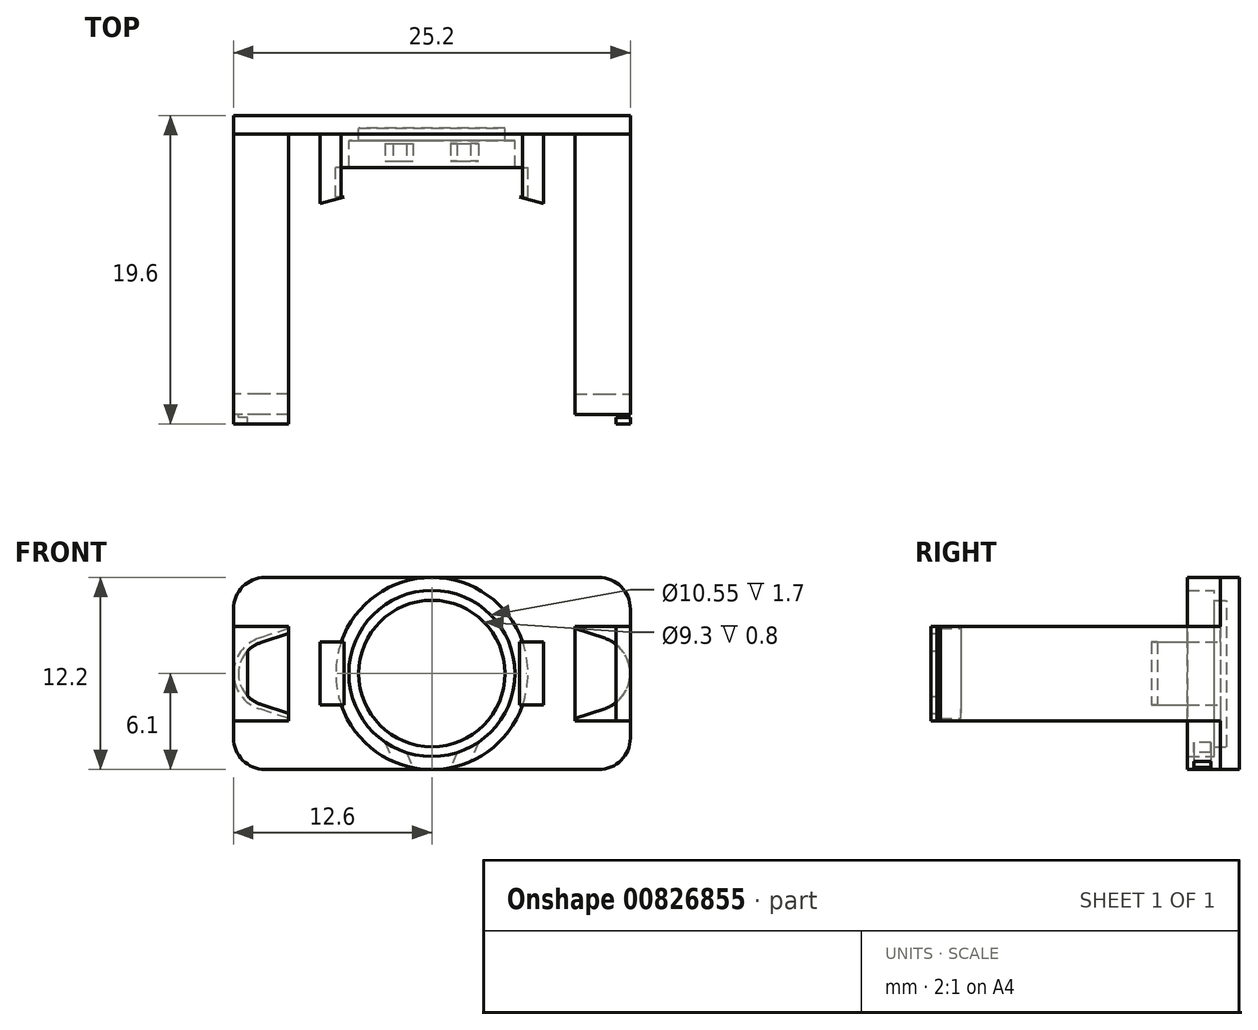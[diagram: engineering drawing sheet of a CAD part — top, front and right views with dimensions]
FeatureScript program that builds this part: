
annotation { "Feature Type Name" : "Feature", "Feature Type Description" : "" }
export const myFeature = defineFeature(function(context is Context, id is Id, definition is map)
    precondition{}
    {
        {
            var Q0;
            Q0=qCreatedBy(makeId("Front.planeOp"),FACE);
            var sketch = newSketch(context, id + "F0", { "sketchPlane" : qUnion([Q0])});
            skCircle(sketch, "E0", {"center": v(0, 0) * mm, "radius": 5 * mm});
            skCircle(sketch, "E1", {"center": v(0, 0) * mm, "radius": 6.1 * mm});
            skSolve(sketch);
        }
        {
            var Q0;
            Q0=makeQuery(id+"F0.imprint","IMPRINT",FACE,{"disambiguationData":[TD([[makeQuery(id+"F0.imprint","IMPRINT",EDGE,{"derivedFrom":sQuery(id+"F0.wireOp",EDGE,"E0")}),-1.0]])]});
            var Q1;
            Q1=makeQuery(id+"F0.imprint","IMPRINT",FACE,{"disambiguationData":[TD([[makeQuery(id+"F0.imprint","IMPRINT",EDGE,{"derivedFrom":sQuery(id+"F0.wireOp",EDGE,"E0")}),1.0]])]});
            extrude(context, id + "F1", {"entities" : qUnion([Q0, Q1]), "depth" : 0.8 * mm, "offsetDistance" : 25 * mm});
        }
        {
            var Q0;
            Q0=makeQuery(id+"F1.opExtrude","CAP_FACE",FACE,{"disambiguationData":[OSD([sQuery(id+"F0.wireOp",EDGE,"E1")])],"isStart":false});
            var sketch = newSketch(context, id + "F2", { "sketchPlane" : qUnion([Q0])});
            skCircle(sketch, "E2", {"center": v(0, 0) * mm, "radius": 5.45 * mm});
            skCircle(sketch, "E3", {"center": v(0, 0) * mm, "radius": 6.1 * mm});
            skSolve(sketch);
        }
        {
            var Q0;
            Q0=makeQuery(id+"F2.imprint","IMPRINT",FACE,{"disambiguationData":[TD([[makeQuery(id+"F2.imprint","IMPRINT",EDGE,{"derivedFrom":sQuery(id+"F2.wireOp",EDGE,"E2")}),-1.0]])]});
            extrude(context, id + "F3", {"entities" : qUnion([Q0]), "operationType" : NewBodyOperationType.ADD, "depth" : 2.5 * mm, "offsetDistance" : 25 * mm});
        }
        {
            var Q0;
            Q0=makeQuery(id+"F1.opExtrude","CAP_FACE",FACE,{"disambiguationData":[OSD([sQuery(id+"F0.wireOp",EDGE,"E1")])],"isStart":false});
            var sketch = newSketch(context, id + "F4", { "sketchPlane" : qUnion([Q0])});
            skCircle(sketch, "E4", {"center": v(0, 0) * mm, "radius": 4.65 * mm});
            skSolve(sketch);
        }
        {
            var Q0;
            Q0=makeQuery(id+"F4.imprint","IMPRINT",FACE,{"disambiguationData":[TD([[makeQuery(id+"F4.imprint","IMPRINT",EDGE,{"derivedFrom":sQuery(id+"F4.wireOp",EDGE,"E4")}),-1.0]])]});
            extrude(context, id + "F5", {"entities" : qUnion([Q0]), "operationType" : NewBodyOperationType.ADD, "depth" : 0.8 * mm, "offsetDistance" : 25 * mm});
        }
        {
            var Q0;
            Q0=makeQuery(id+"F5.opExtrude","CAP_FACE",FACE,{"disambiguationData":[OSD([sQuery(id+"F2.wireOp",EDGE,"E2"),sQuery(id+"F4.wireOp",EDGE,"E4")])],"isStart":false});
            var sketch = newSketch(context, id + "F6", { "sketchPlane" : qUnion([Q0])});
            skCircle(sketch, "E5", {"center": v(0, 0) * mm, "radius": 5.28 * mm});
            skSolve(sketch);
        }
        {
            var Q0;
            Q0=makeQuery(id+"F6.imprint","IMPRINT",FACE,{"disambiguationData":[TD([[makeQuery(id+"F6.imprint","IMPRINT",EDGE,{"derivedFrom":sQuery(id+"F6.wireOp",EDGE,"E5")}),-1.0]])]});
            extrude(context, id + "F7", {"entities" : qUnion([Q0]), "operationType" : NewBodyOperationType.ADD, "depth" : 1.7 * mm, "offsetDistance" : 25 * mm});
        }
        {
            var Q0;
            Q0=makeQuery(id+"F3.opExtrude","CAP_FACE",FACE,{"disambiguationData":[OSD([sQuery(id+"F2.wireOp",EDGE,"E2"),sQuery(id+"F2.wireOp",EDGE,"E3")])],"isStart":false});
            var sketch = newSketch(context, id + "F8", { "sketchPlane" : qUnion([Q0])});
            skLineSegment(sketch, "E6", {"start": v(-1.6, -5.03) * mm, "end": v(-1.2, -5.98) * mm});
            skLineSegment(sketch, "E7", {"start": v(-2.96, -4.37) * mm, "end": v(-2.45, -5.59) * mm});
            skLineSegment(sketch, "E8.MirrorCS", {"start": v(1.6, -5.03) * mm, "end": v(1.2, -5.98) * mm});
            skLineSegment(sketch, "E9.MirrorCS", {"start": v(2.96, -4.37) * mm, "end": v(2.45, -5.59) * mm});
            skSolve(sketch);
        }
        {
            var Q0;
            {var subQ0=sQuery(id+"F8.wireOp",EDGE,"E6");Q0=makeQuery(id+"F8.imprint","IMPRINT",FACE,{"disambiguationData":[TD([[makeQuery(id+"F8.imprint","IMPRINT",EDGE,{"derivedFrom":subQ0}),-1.0]])]});}
            var Q1;
            {var subQ0=sQuery(id+"F8.wireOp",EDGE,"E8.MirrorCS");Q1=makeQuery(id+"F8.imprint","IMPRINT",FACE,{"disambiguationData":[TD([[makeQuery(id+"F8.imprint","IMPRINT",EDGE,{"derivedFrom":subQ0}),1.0]])]});}
            extrude(context, id + "F9", {"entities" : qUnion([Q0, Q1]), "operationType" : NewBodyOperationType.REMOVE, "oppositeDirection" : true, "depth" : 1.5 * mm, "offsetDistance" : 25 * mm});
        }
        {
            var Q0;
            {var subQ0=sQuery(id+"F2.wireOp",EDGE,"E3");var subQ1=sQuery(id+"F2.wireOp",EDGE,"E2");Q0=makeQuery(id+"F9.boolean.opBoolean","SPLIT",FACE,{"disambiguationData":[TD([makeQuery(id+"F9.opExtrude","SWEPT_FACE",FACE,{"disambiguationData":[OSD([sQuery(id+"F8.wireOp",EDGE,"E7")])]})])],"derivedFrom":makeQuery(id+"F3.opExtrude","CAP_FACE",FACE,{"disambiguationData":[OSD([subQ1,subQ0])],"isStart":false})});}
            var sketch = newSketch(context, id + "F10", { "sketchPlane" : qUnion([Q0])});
            skArc(sketch, "E10", {"start": v(-2.45, -5.59) * mm, "mid": v(-1.84, -5.82) * mm, "end": v(-1.2, -5.98) * mm});
            skLineSegment(sketch, "E11", {"start": v(-2.96, -4.37) * mm, "end": v(-2.45, -5.59) * mm});
            skLineSegment(sketch, "E12", {"start": v(-1.6, -5.03) * mm, "end": v(-1.2, -5.98) * mm});
            skLineSegment(sketch, "E13.MirrorCS", {"start": v(2.96, -4.37) * mm, "end": v(2.45, -5.59) * mm});
            skArc(sketch, "E14.MirrorCS", {"start": v(2.45, -5.59) * mm, "mid": v(1.84, -5.82) * mm, "end": v(1.2, -5.98) * mm});
            skLineSegment(sketch, "E15.MirrorCS", {"start": v(1.6, -5.03) * mm, "end": v(1.2, -5.98) * mm});
            skPoint(sketch, "E16.MirrorCS.end.orphan", {"position": v(1.6, -5.03) * mm});
            skPoint(sketch, "E16.MirrorCS.start.orphan", {"position": v(2.96, -4.37) * mm});
            skPoint(sketch, "E17.MirrorCS.end.orphan", {"position": v(-2.96, -4.37) * mm});
            skPoint(sketch, "E17.MirrorCS.start.orphan", {"position": v(-1.6, -5.03) * mm});
            skSolve(sketch);
        }
        {
            var Q0;
            {var subQ0=sQuery(id+"F8.wireOp",EDGE,"E6");Q0=makeQuery(id+"F8.imprint","IMPRINT",FACE,{"disambiguationData":[TD([[makeQuery(id+"F8.imprint","IMPRINT",EDGE,{"derivedFrom":subQ0}),-1.0]])]});}
            var Q1;
            {var subQ0=sQuery(id+"F8.wireOp",EDGE,"E8.MirrorCS");Q1=makeQuery(id+"F8.imprint","IMPRINT",FACE,{"disambiguationData":[TD([[makeQuery(id+"F8.imprint","IMPRINT",EDGE,{"derivedFrom":subQ0}),1.0]])]});}
            extrude(context, id + "F11", {"entities" : qUnion([Q0, Q1]), "operationType" : NewBodyOperationType.ADD, "oppositeDirection" : true, "depth" : 0.4 * mm, "offsetDistance" : 25 * mm});
        }
        {
            var Q0;
            Q0=makeQuery(id+"F1.opExtrude","CAP_FACE",FACE,{"disambiguationData":[OSD([sQuery(id+"F0.wireOp",EDGE,"E1")])],"isStart":true});
            var sketch = newSketch(context, id + "F12", { "sketchPlane" : qUnion([Q0])});
            skLineSegment(sketch, "E18.bottom", {"start": v(-12.6, -6.1) * mm, "end": v(12.6, -6.1) * mm});
            skLineSegment(sketch, "E18.top", {"start": v(-12.6, 6.1) * mm, "end": v(12.6, 6.1) * mm});
            skLineSegment(sketch, "E18.left", {"start": v(-12.6, -6.1) * mm, "end": v(-12.6, 6.1) * mm});
            skLineSegment(sketch, "E18.right", {"start": v(12.6, -6.1) * mm, "end": v(12.6, 6.1) * mm});
            skPoint(sketch, "E18.middle", {"position": v(0, 0) * mm});
            skSolve(sketch);
        }
        {
            var Q0;
            {var subQ0=sQuery(id+"F12.wireOp",EDGE,"E18.right");Q0=makeQuery(id+"F12.imprint","IMPRINT",FACE,{"disambiguationData":[TD([[makeQuery(id+"F12.imprint","IMPRINT",EDGE,{"derivedFrom":subQ0}),1.0]])]});}
            var Q1;
            {var subQ0=sQuery(id+"F12.wireOp",EDGE,"E18.left");Q1=makeQuery(id+"F12.imprint","IMPRINT",FACE,{"disambiguationData":[TD([[makeQuery(id+"F12.imprint","IMPRINT",EDGE,{"derivedFrom":subQ0}),-1.0]])]});}
            extrude(context, id + "F13", {"entities" : qUnion([Q0, Q1]), "operationType" : NewBodyOperationType.ADD, "oppositeDirection" : true, "depth" : 1.2 * mm, "offsetDistance" : 25 * mm});
        }
        {
            var Q0;
            Q0=makeQuery(id+"F13.opExtrude","SWEPT_EDGE",EDGE,{"disambiguationData":[OSD([sQuery(id+"F12.wireOp",EDGE,"E18.bottom"),sQuery(id+"F12.wireOp",EDGE,"E18.right")])]});
            var Q1;
            Q1=makeQuery(id+"F13.opExtrude","SWEPT_EDGE",EDGE,{"disambiguationData":[OSD([sQuery(id+"F12.wireOp",EDGE,"E18.bottom"),sQuery(id+"F12.wireOp",EDGE,"E18.left")])]});
            var Q2;
            Q2=makeQuery(id+"F13.opExtrude","SWEPT_EDGE",EDGE,{"disambiguationData":[OSD([sQuery(id+"F12.wireOp",EDGE,"E18.top"),sQuery(id+"F12.wireOp",EDGE,"E18.left")])]});
            var Q3;
            Q3=makeQuery(id+"F13.opExtrude","SWEPT_EDGE",EDGE,{"disambiguationData":[OSD([sQuery(id+"F12.wireOp",EDGE,"E18.top"),sQuery(id+"F12.wireOp",EDGE,"E18.right")])]});
            fillet(context, id + "F14", {"entities" : qUnion([Q0, Q1, Q2, Q3]), "radius" : 2 * mm, "tangentPropagation" : true, "allowEdgeOverflow" : false});
        }
        {
            var Q0;
            Q0=makeQuery(id+"F13.opExtrude","CAP_FACE",FACE,{"disambiguationData":[OSD([sQuery(id+"F0.wireOp",EDGE,"E1"),sQuery(id+"F12.wireOp",EDGE,"E18.bottom"),sQuery(id+"F12.wireOp",EDGE,"E18.top"),sQuery(id+"F12.wireOp",EDGE,"E18.right")])],"isStart":false});
            var sketch = newSketch(context, id + "F15", { "sketchPlane" : qUnion([Q0])});
            skLineSegment(sketch, "E19", {"start": v(-12.6, 3) * mm, "end": v(-9.1, 3) * mm});
            skLineSegment(sketch, "E20", {"start": v(-9.1, 3) * mm, "end": v(-9.1, -3) * mm});
            skLineSegment(sketch, "E21", {"start": v(-9.1, -3) * mm, "end": v(-12.6, -3) * mm});
            skLineSegment(sketch, "E22", {"start": v(-7.1, 2) * mm, "end": v(-7.1, -2) * mm});
            skLineSegment(sketch, "E23", {"start": v(-7.1, -2) * mm, "end": v(-5.76, -2) * mm});
            skLineSegment(sketch, "E24", {"start": v(-7.1, 2) * mm, "end": v(-5.76, 2) * mm});
            skSolve(sketch);
        }
        {
            var Q0;
            {var subQ0=sQuery(id+"F15.wireOp",EDGE,"E19");Q0=makeQuery(id+"F15.imprint","IMPRINT",FACE,{"disambiguationData":[TD([[makeQuery(id+"F15.imprint","IMPRINT",EDGE,{"derivedFrom":subQ0}),-1.0]])]});}
            extrude(context, id + "F16", {"entities" : qUnion([Q0]), "operationType" : NewBodyOperationType.ADD, "depth" : 16.5 * mm, "offsetDistance" : 25 * mm});
        }
        {
            var Q0;
            Q0=makeQuery(id+"F13.opExtrude","CAP_FACE",FACE,{"disambiguationData":[OSD([sQuery(id+"F0.wireOp",EDGE,"E1"),sQuery(id+"F12.wireOp",EDGE,"E18.bottom"),sQuery(id+"F12.wireOp",EDGE,"E18.top"),sQuery(id+"F12.wireOp",EDGE,"E18.left")])],"isStart":false});
            var sketch = newSketch(context, id + "F17", { "sketchPlane" : qUnion([Q0])});
            skLineSegment(sketch, "E25", {"start": v(12.6, 3) * mm, "end": v(9.1, 3) * mm});
            skLineSegment(sketch, "E26", {"start": v(9.1, 3) * mm, "end": v(9.1, -3) * mm});
            skLineSegment(sketch, "E27", {"start": v(9.1, -3) * mm, "end": v(12.6, -3) * mm});
            skLineSegment(sketch, "E28", {"start": v(7.1, 2) * mm, "end": v(7.1, -2) * mm});
            skLineSegment(sketch, "E29", {"start": v(7.1, -2) * mm, "end": v(5.76, -2) * mm});
            skLineSegment(sketch, "E30", {"start": v(7.1, 2) * mm, "end": v(5.76, 2) * mm});
            skSolve(sketch);
        }
        {
            var Q0;
            {var subQ0=sQuery(id+"F17.wireOp",EDGE,"E25");Q0=makeQuery(id+"F17.imprint","IMPRINT",FACE,{"disambiguationData":[TD([[makeQuery(id+"F17.imprint","IMPRINT",EDGE,{"derivedFrom":subQ0}),1.0]])]});}
            extrude(context, id + "F18", {"entities" : qUnion([Q0]), "operationType" : NewBodyOperationType.ADD, "depth" : 16.5 * mm, "offsetDistance" : 25 * mm});
        }
        {
            var Q0;
            Q0=makeQuery(id+"F17.imprint","IMPRINT",FACE,{"disambiguationData":[TD([[makeQuery(id+"F17.imprint","IMPRINT",EDGE,{"derivedFrom":sQuery(id+"F17.wireOp",EDGE,"E28")}),-1.0]])]});
            var Q1;
            Q1=makeQuery(id+"F15.imprint","IMPRINT",FACE,{"disambiguationData":[TD([[makeQuery(id+"F15.imprint","IMPRINT",EDGE,{"derivedFrom":sQuery(id+"F15.wireOp",EDGE,"E22")}),1.0]])]});
            extrude(context, id + "F19", {"entities" : qUnion([Q0, Q1]), "operationType" : NewBodyOperationType.ADD, "depth" : 4 * mm, "offsetDistance" : 25 * mm});
        }
        {
            var Q0;
            Q0=makeQuery(id+"F19.opExtrude","SWEPT_FACE",FACE,{"disambiguationData":[OSD([sQuery(id+"F15.wireOp",EDGE,"E23")])]});
            var sketch = newSketch(context, id + "F20", { "sketchPlane" : qUnion([Q0])});
            skLineSegment(sketch, "E31", {"start": v(-7.1, 5.2) * mm, "end": v(-7.1, 5.6) * mm});
            skLineSegment(sketch, "E32", {"start": v(-5.76, 5.2) * mm, "end": v(-5.66, 5.2) * mm});
            skLineSegment(sketch, "E33", {"start": v(-5.66, 5.2) * mm, "end": v(-7.1, 5.6) * mm});
            skSolve(sketch);
        }
        {
            var Q0;
            Q0=makeQuery(id+"F20.imprint","IMPRINT",FACE,{"disambiguationData":[TD([[makeQuery(id+"F20.imprint","IMPRINT",EDGE,{"derivedFrom":sQuery(id+"F20.wireOp",EDGE,"E31")}),-1.0]])]});
            extrude(context, id + "F21", {"entities" : qUnion([Q0]), "operationType" : NewBodyOperationType.ADD, "oppositeDirection" : true, "depth" : 4 * mm, "offsetDistance" : 25 * mm});
        }
        {
            var Q0;
            Q0=makeQuery(id+"F19.opExtrude","SWEPT_FACE",FACE,{"disambiguationData":[OSD([sQuery(id+"F17.wireOp",EDGE,"E29")])]});
            var sketch = newSketch(context, id + "F22", { "sketchPlane" : qUnion([Q0])});
            skLineSegment(sketch, "E34", {"start": v(7.1, 5.2) * mm, "end": v(7.1, 5.6) * mm});
            skLineSegment(sketch, "E35", {"start": v(5.76, 5.2) * mm, "end": v(5.66, 5.2) * mm});
            skLineSegment(sketch, "E36", {"start": v(5.66, 5.2) * mm, "end": v(7.1, 5.6) * mm});
            skSolve(sketch);
        }
        {
            var Q0;
            Q0=makeQuery(id+"F22.imprint","IMPRINT",FACE,{"disambiguationData":[TD([[makeQuery(id+"F22.imprint","IMPRINT",EDGE,{"derivedFrom":sQuery(id+"F22.wireOp",EDGE,"E34")}),1.0]])]});
            extrude(context, id + "F23", {"entities" : qUnion([Q0]), "operationType" : NewBodyOperationType.ADD, "oppositeDirection" : true, "depth" : 4 * mm, "offsetDistance" : 25 * mm});
        }
        {
            var Q0;
            {var subQ0=sQuery(id+"F15.wireOp",EDGE,"E23");Q0=makeQuery(id+"F21.boolean.opBoolean","MERGE",FACE,{"derivedFrom":[makeQuery(id+"F19.opExtrude","SWEPT_FACE",FACE,{"disambiguationData":[OSD([subQ0])]}),makeQuery(id+"F21.opExtrude","CAP_FACE",FACE,{"disambiguationData":[OSD([subQ0,sQuery(id+"F20.wireOp",EDGE,"E31"),sQuery(id+"F20.wireOp",EDGE,"scbSYdZa-IKE8-HjIA-PmpS-5iz6sRiiHXsu")])],"isStart":true})]});}
            var sketch = newSketch(context, id + "F24", { "sketchPlane" : qUnion([Q0])});
            skLineSegment(sketch, "E37", {"start": v(-5.76, 5.2) * mm, "end": v(-5.56, 5.2) * mm});
            skLineSegment(sketch, "E38", {"start": v(-5.56, 5.2) * mm, "end": v(-7.1, 5.6) * mm});
            skSolve(sketch);
        }
        {
            var Q0;
            Q0=makeQuery(id+"F24.imprint","IMPRINT",FACE,{"disambiguationData":[TD([[makeQuery(id+"F24.imprint","IMPRINT",EDGE,{"derivedFrom":sQuery(id+"F24.wireOp",EDGE,"E37")}),1.0]])]});
            extrude(context, id + "F25", {"entities" : qUnion([Q0]), "operationType" : NewBodyOperationType.ADD, "oppositeDirection" : true, "depth" : 4 * mm, "offsetDistance" : 25 * mm});
        }
        {
            var Q0;
            {var subQ0=sQuery(id+"F17.wireOp",EDGE,"E29");Q0=makeQuery(id+"F23.boolean.opBoolean","MERGE",FACE,{"derivedFrom":[makeQuery(id+"F19.opExtrude","SWEPT_FACE",FACE,{"disambiguationData":[OSD([subQ0])]}),makeQuery(id+"F23.opExtrude","CAP_FACE",FACE,{"disambiguationData":[OSD([subQ0,sQuery(id+"F22.wireOp",EDGE,"E34"),sQuery(id+"F22.wireOp",EDGE,"OUZQXp2e-nWsZ-sgYy-KXVV-Yu3MqT17kAb9")])],"isStart":true})]});}
            var sketch = newSketch(context, id + "F26", { "sketchPlane" : qUnion([Q0])});
            skLineSegment(sketch, "E39", {"start": v(5.76, 5.2) * mm, "end": v(5.56, 5.2) * mm});
            skLineSegment(sketch, "E40", {"start": v(5.56, 5.2) * mm, "end": v(7.1, 5.6) * mm});
            skSolve(sketch);
        }
        {
            var Q0;
            Q0=makeQuery(id+"F26.imprint","IMPRINT",FACE,{"disambiguationData":[TD([[makeQuery(id+"F26.imprint","IMPRINT",EDGE,{"derivedFrom":sQuery(id+"F26.wireOp",EDGE,"E39")}),-1.0]])]});
            extrude(context, id + "F27", {"entities" : qUnion([Q0]), "operationType" : NewBodyOperationType.ADD, "oppositeDirection" : true, "depth" : 4 * mm, "offsetDistance" : 25 * mm});
        }
        {
            var Q0;
            Q0=makeQuery(id+"F18.opExtrude","CAP_FACE",FACE,{"disambiguationData":[OSD([sQuery(id+"F12.wireOp",EDGE,"E18.left"),sQuery(id+"F17.wireOp",EDGE,"E25"),sQuery(id+"F17.wireOp",EDGE,"E26"),sQuery(id+"F17.wireOp",EDGE,"E27")])],"isStart":false});
            var sketch = newSketch(context, id + "F28", { "sketchPlane" : qUnion([Q0])});
            skLineSegment(sketch, "E41", {"start": v(9.1, 2.85) * mm, "end": v(10.95, 2.25) * mm});
            skArc(sketch, "E42", {"start": v(10.95, -2.25) * mm, "mid": v(12.59, 0) * mm, "end": v(10.95, 2.25) * mm});
            skLineSegment(sketch, "E43.MirrorCS", {"start": v(9.1, -2.85) * mm, "end": v(10.95, -2.25) * mm});
            skSolve(sketch);
        }
        {
            var Q0;
            {var subQ2=sQuery(id+"F28.wireOp",EDGE,"E41");Q0=makeQuery(id+"F28.imprint","IMPRINT",FACE,{"disambiguationData":[TD([[makeQuery(id+"F28.imprint","IMPRINT",EDGE,{"derivedFrom":subQ2}),1.0]])]});}
            extrude(context, id + "F29", {"entities" : qUnion([Q0]), "operationType" : NewBodyOperationType.ADD, "depth" : 1.3 * mm, "offsetDistance" : 25 * mm});
        }
        {
            var Q0;
            Q0=makeQuery(id+"F16.opExtrude","CAP_FACE",FACE,{"disambiguationData":[OSD([sQuery(id+"F12.wireOp",EDGE,"E18.right"),sQuery(id+"F15.wireOp",EDGE,"E19"),sQuery(id+"F15.wireOp",EDGE,"E20"),sQuery(id+"F15.wireOp",EDGE,"E21")])],"isStart":false});
            var sketch = newSketch(context, id + "F30", { "sketchPlane" : qUnion([Q0])});
            skLineSegment(sketch, "E44", {"start": v(-9.1, 2.85) * mm, "end": v(-10.95, 2.25) * mm});
            skLineSegment(sketch, "E45.MirrorCS", {"start": v(-9.1, -2.85) * mm, "end": v(-10.95, -2.25) * mm});
            skArc(sketch, "E46", {"start": v(-10.95, 2.25) * mm, "mid": v(-12.59, 0) * mm, "end": v(-10.95, -2.25) * mm});
            skSolve(sketch);
        }
        {
            var Q0;
            {var subQ2=sQuery(id+"F30.wireOp",EDGE,"E44");Q0=makeQuery(id+"F30.imprint","IMPRINT",FACE,{"disambiguationData":[TD([[makeQuery(id+"F30.imprint","IMPRINT",EDGE,{"derivedFrom":subQ2}),-1.0]])]});}
            extrude(context, id + "F31", {"entities" : qUnion([Q0]), "operationType" : NewBodyOperationType.ADD, "depth" : 1.3 * mm, "offsetDistance" : 25 * mm});
        }
        {
            var Q0;
            Q0=makeQuery(id+"F31.opExtrude","CAP_FACE",FACE,{"disambiguationData":[OSD([sQuery(id+"F12.wireOp",EDGE,"E18.right"),sQuery(id+"F15.wireOp",EDGE,"E19"),sQuery(id+"F15.wireOp",EDGE,"E20"),sQuery(id+"F15.wireOp",EDGE,"E21"),sQuery(id+"F30.wireOp",EDGE,"E44"),sQuery(id+"F30.wireOp",EDGE,"E45.MirrorCS"),sQuery(id+"F30.wireOp",EDGE,"E46")])],"isStart":false});
            var sketch = newSketch(context, id + "F32", { "sketchPlane" : qUnion([Q0])});
            skLineSegment(sketch, "E47", {"start": v(-12.6, 3) * mm, "end": v(-12.6, -3) * mm});
            skLineSegment(sketch, "E48", {"start": v(-12.6, -3) * mm, "end": v(-9.1, -3) * mm});
            skLineSegment(sketch, "E49.0", {"start": v(-9.1, -2.53) * mm, "end": v(-10.86, -1.96) * mm});
            skArc(sketch, "E49.1", {"start": v(-10.86, 1.96) * mm, "mid": v(-12.3, 0) * mm, "end": v(-10.86, -1.96) * mm});
            skLineSegment(sketch, "E49.2", {"start": v(-9.1, 2.53) * mm, "end": v(-10.86, 1.96) * mm});
            skArc(sketch, "E50.MirrorCS", {"start": v(10.86, 1.96) * mm, "mid": v(12.3, 0) * mm, "end": v(10.86, -1.96) * mm});
            skLineSegment(sketch, "E51.MirrorCS", {"start": v(9.1, 2.53) * mm, "end": v(10.86, 1.96) * mm});
            skLineSegment(sketch, "E52.MirrorCS", {"start": v(9.1, -2.53) * mm, "end": v(10.86, -1.96) * mm});
            skLineSegment(sketch, "E53.MirrorCS", {"start": v(12.6, -3) * mm, "end": v(9.1, -3) * mm});
            skLineSegment(sketch, "E54.MirrorCS", {"start": v(12.6, 3) * mm, "end": v(12.6, -3) * mm});
            skLineSegment(sketch, "E55", {"start": v(-12.6, 3) * mm, "end": v(-9.1, 3) * mm});
            skLineSegment(sketch, "E56.MirrorCS", {"start": v(12.6, 3) * mm, "end": v(9.1, 3) * mm});
            skLineSegment(sketch, "E57", {"start": v(-9.1, 2.53) * mm, "end": v(-9.1, 3) * mm});
            skLineSegment(sketch, "E58", {"start": v(-9.1, -2.53) * mm, "end": v(-9.1, -3) * mm});
            skLineSegment(sketch, "E59.MirrorCS", {"start": v(9.1, -2.53) * mm, "end": v(9.1, -3) * mm});
            skLineSegment(sketch, "E60.MirrorCS", {"start": v(9.1, 2.53) * mm, "end": v(9.1, 3) * mm});
            skSolve(sketch);
        }
        {
            var Q0;
            {var subQ3=sQuery(id+"F32.wireOp",EDGE,"E49.0");Q0=makeQuery(id+"F32.imprint","IMPRINT",FACE,{"disambiguationData":[TD([[makeQuery(id+"F32.imprint","IMPRINT",EDGE,{"derivedFrom":subQ3}),1.0]])]});}
            var Q1;
            Q1=makeQuery(id+"F32.imprint","IMPRINT",FACE,{"disambiguationData":[TD([[makeQuery(id+"F32.imprint","IMPRINT",EDGE,{"derivedFrom":sQuery(id+"F32.wireOp",EDGE,"E47")}),-1.0]])]});
            var Q2;
            Q2=makeQuery(id+"F32.imprint","IMPRINT",FACE,{"disambiguationData":[TD([[makeQuery(id+"F32.imprint","IMPRINT",EDGE,{"derivedFrom":sQuery(id+"F32.wireOp",EDGE,"E50.MirrorCS")}),1.0]])]});
            extrude(context, id + "F33", {"entities" : qUnion([Q0, Q1, Q2]), "operationType" : NewBodyOperationType.ADD, "depth" : 0.2 * mm, "offsetDistance" : 25 * mm});
        }
        {
            var Q0;
            Q0=makeQuery(id+"F33.opExtrude","CAP_FACE",FACE,{"disambiguationData":[OSD([sQuery(id+"F32.wireOp",EDGE,"E47"),sQuery(id+"F32.wireOp",EDGE,"E48"),sQuery(id+"F32.wireOp",EDGE,"E49.0"),sQuery(id+"F32.wireOp",EDGE,"E49.1"),sQuery(id+"F32.wireOp",EDGE,"E49.2"),sQuery(id+"F32.wireOp",EDGE,"E55"),sQuery(id+"F32.wireOp",EDGE,"E57"),sQuery(id+"F32.wireOp",EDGE,"E58")])],"isStart":false});
            var sketch = newSketch(context, id + "F34", { "sketchPlane" : qUnion([Q0])});
            skLineSegment(sketch, "E61.bottom", {"start": v(-12.6, 3) * mm, "end": v(-11.7, 3) * mm});
            skLineSegment(sketch, "E61.top", {"start": v(-12.6, -3) * mm, "end": v(-11.7, -3) * mm});
            skLineSegment(sketch, "E61.left", {"start": v(-12.6, 3) * mm, "end": v(-12.6, -3) * mm});
            skLineSegment(sketch, "E61.right", {"start": v(-11.7, 3) * mm, "end": v(-11.7, -3) * mm});
            skLineSegment(sketch, "E62.MirrorCS", {"start": v(11.7, 3) * mm, "end": v(11.7, -3) * mm});
            skLineSegment(sketch, "E63.MirrorCS", {"start": v(12.6, 3) * mm, "end": v(12.6, -3) * mm});
            skLineSegment(sketch, "E64.MirrorCS", {"start": v(12.6, 3) * mm, "end": v(11.7, 3) * mm});
            skLineSegment(sketch, "E65.MirrorCS", {"start": v(12.6, -3) * mm, "end": v(11.7, -3) * mm});
            skSolve(sketch);
        }
        {
            var Q0;
            {var subQ1=sQuery(id+"F34.wireOp",EDGE,"E61.bottom");Q0=makeQuery(id+"F34.imprint","IMPRINT",FACE,{"disambiguationData":[TD([[makeQuery(id+"F34.imprint","IMPRINT",EDGE,{"derivedFrom":subQ1}),-1.0]])]});}
            var Q1;
            {var subQ0=sQuery(id+"F34.wireOp",EDGE,"E61.right");var subQ1=makeQuery(id+"F33.opExtrude","CAP_EDGE",EDGE,{"disambiguationData":[OSD([sQuery(id+"F32.wireOp",EDGE,"E49.1")])],"isStart":false});var subQ2=makeQuery(id+"F34.imprint","INTERSECT",VERTEX,{"disambiguationData":[OD(0.0)],"derivedFrom":[subQ1,subQ0]});Q1=makeQuery(id+"F34.imprint","IMPRINT",FACE,{"disambiguationData":[TD([[makeQuery(id+"F34.imprint","IMPRINT",EDGE,{"disambiguationData":[TD([[subQ2,-1.0]])],"derivedFrom":subQ0}),-1.0]])]});}
            var Q2;
            Q2=makeQuery(id+"F34.imprint","IMPRINT",FACE,{"disambiguationData":[TD([[makeQuery(id+"F34.imprint","IMPRINT",EDGE,{"derivedFrom":sQuery(id+"F34.wireOp",EDGE,"E62.MirrorCS")}),1.0]])]});
            var Q3;
            {var subQ6=makeQuery(id+"F33.opExtrude","CAP_EDGE",EDGE,{"disambiguationData":[OSD([sQuery(id+"F32.wireOp",EDGE,"E49.2")])],"isStart":false});Q3=makeQuery(id+"F34.imprint","IMPRINT",FACE,{"disambiguationData":[TD([[makeQuery(id+"F34.imprint","IMPRINT",EDGE,{"derivedFrom":subQ6}),-1.0]])]});}
            var Q4;
            {var subQ0=makeQuery(id+"F33.opExtrude","CAP_EDGE",EDGE,{"disambiguationData":[OSD([sQuery(id+"F32.wireOp",EDGE,"E49.0")])],"isStart":false});Q4=makeQuery(id+"F34.imprint","IMPRINT",FACE,{"disambiguationData":[TD([[makeQuery(id+"F34.imprint","IMPRINT",EDGE,{"derivedFrom":subQ0}),1.0]])]});}
            var Q5;
            Q5=makeQuery(id+"F33.opExtrude","CAP_FACE",FACE,{"disambiguationData":[OSD([sQuery(id+"F32.wireOp",EDGE,"E50.MirrorCS"),sQuery(id+"F32.wireOp",EDGE,"E51.MirrorCS"),sQuery(id+"F32.wireOp",EDGE,"E52.MirrorCS"),sQuery(id+"F32.wireOp",EDGE,"E53.MirrorCS"),sQuery(id+"F32.wireOp",EDGE,"E54.MirrorCS"),sQuery(id+"F32.wireOp",EDGE,"E56.MirrorCS"),sQuery(id+"F32.wireOp",EDGE,"E59.MirrorCS"),sQuery(id+"F32.wireOp",EDGE,"E60.MirrorCS")])],"isStart":false});
            extrude(context, id + "F35", {"entities" : qUnion([Q0, Q1, Q2, Q3, Q4, Q5]), "operationType" : NewBodyOperationType.ADD, "depth" : 0.4 * mm, "offsetDistance" : 25 * mm});
        }
    });
